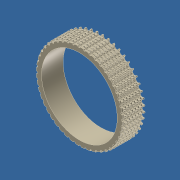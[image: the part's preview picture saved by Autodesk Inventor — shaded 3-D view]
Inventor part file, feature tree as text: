
AUTODESK INVENTOR PART (.ipt)
format: ipt  version: unknown  size: 3,829,248 bytes
history: native  units: in
note: dims shown in document units (in); Inventor stores cm internally (conversion verified against a paired STEP export)
features: extrude x2, sketch x2, pattern_circular x1, pattern_linear x1
ambient origin geometry x8: Origin, YZ Plane, XZ Plane, XY Plane, X Axis, Y Axis, Z Axis, Center Point
bodies: Solid1 (feature_tree)
feature tree (6):
  extrude  "Extrusion1"  Depth=0.05in
  extrude  "Extrusion2"  Depth=2.0in
  pattern_circular  "Circular Pattern2"  [2 undecoded]
  pattern_linear  "Rectangular Pattern1"  Spacing1=0.292in  [1 undecoded]
  sketch  "Sketch1"  dims[d0=0.0515in d1=0.05in]
  sketch  "Sketch2"  dims[d2=0.05in d3=2.0in d4=0.0714in d5=0.0in d6=0.292in d7=0.106in d9=0.106in d10=0.0714in d11=0.0in d15=18.8976in d16=360.0deg d18=2.7559in d20=0.1429in]
note: 3 required parameter values undecoded (feature->parameter linkage not recoverable at this tier; creation-order binding heuristic only, values carry confidence <= 0.55)
